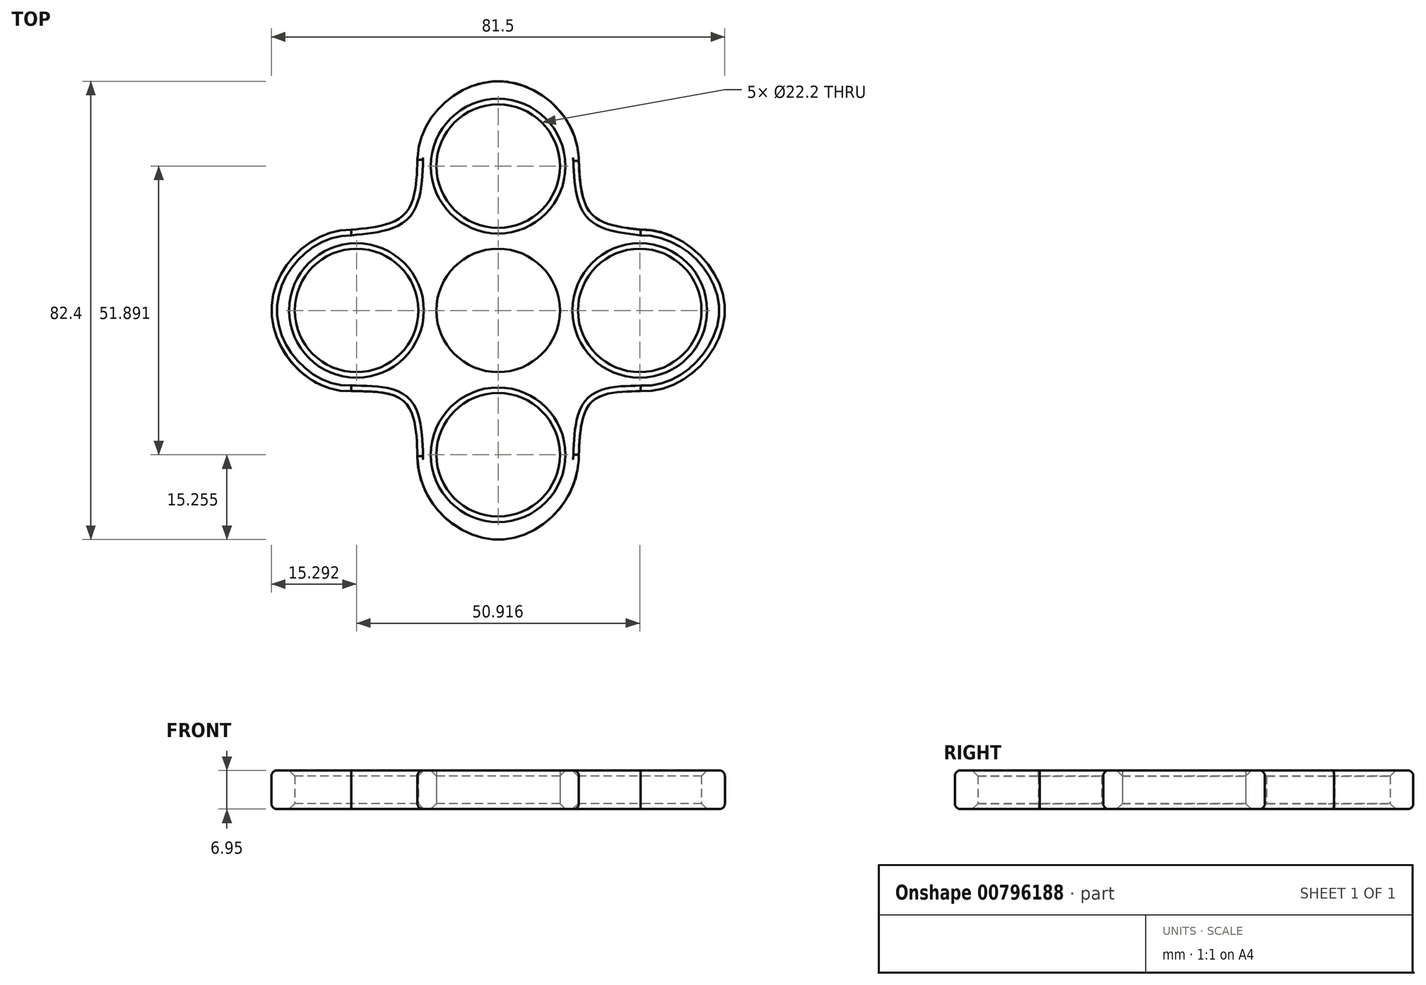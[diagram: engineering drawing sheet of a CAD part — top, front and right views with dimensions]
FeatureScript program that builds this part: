
annotation { "Feature Type Name" : "Feature", "Feature Type Description" : "" }
export const myFeature = defineFeature(function(context is Context, id is Id, definition is map)
    precondition{}
    {
        {
            var Q0;
            Q0=qCreatedBy(makeId("Top.planeOp"),FACE);
            var sketch = newSketch(context, id + "F0", { "sketchPlane" : qUnion([Q0])});
            skCircle(sketch, "E0", {"center": v(0, 0) * mm, "radius": 11.1 * mm});
            skCircle(sketch, "E1", {"center": v(-25.46, 0) * mm, "radius": 11.1 * mm});
            skCircle(sketch, "E2.MirrorC", {"center": v(25.46, 0) * mm, "radius": 11.1 * mm});
            skCircle(sketch, "E3", {"center": v(0, 25.95) * mm, "radius": 11.1 * mm});
            skCircle(sketch, "E4.MirrorC", {"center": v(0, -25.95) * mm, "radius": 11.1 * mm});
            skSolve(sketch);
        }
        {
            var Q0;
            Q0=qCreatedBy(makeId("Top.planeOp"),FACE);
            var sketch = newSketch(context, id + "F1", { "sketchPlane" : qUnion([Q0])});
            skPoint(sketch, "E5", {"position": v(-26.41, 14.52) * mm});
            skPoint(sketch, "E6", {"position": v(25.62, 14.52) * mm});
            skPoint(sketch, "E7.MirrorP", {"position": v(-26.41, -14.52) * mm});
            skPoint(sketch, "E8.MirrorP", {"position": v(25.62, -14.52) * mm});
            skPoint(sketch, "E9", {"position": v(0, 41.2) * mm});
            skPoint(sketch, "E10.MirrorP", {"position": v(0, -41.2) * mm});
            skPoint(sketch, "E11", {"position": v(-40.75, 0) * mm});
            skPoint(sketch, "E12.MirrorP", {"position": v(40.75, 0) * mm});
            skPoint(sketch, "E13", {"position": v(14.49, 27.53) * mm});
            skPoint(sketch, "E14", {"position": v(14.49, -26.88) * mm});
            skPoint(sketch, "E15.MirrorP", {"position": v(-14.49, 27.53) * mm});
            skPoint(sketch, "E16.MirrorP", {"position": v(-14.49, -26.88) * mm});
            skPoint(sketch, "E17", {"position": v(-10.43, 9.88) * mm});
            skPoint(sketch, "E18", {"position": v(10.75, 9.88) * mm});
            skPoint(sketch, "E19", {"position": v(-10.43, -8.6) * mm});
            skPoint(sketch, "E20", {"position": v(10.75, -8.4) * mm});
            skFitSpline(sketch, "E21", {"points": [v(-40.75, 0) * mm, v(-26.41, 14.52) * mm, v(-10.43, 9.88) * mm, v(-14.49, 27.53) * mm, v(0, 41.2) * mm, v(14.49, 27.53) * mm, v(10.75, 9.88) * mm, v(25.62, 14.52) * mm, v(40.75, 0) * mm, v(25.62, -14.52) * mm, v(10.75, -8.4) * mm, v(14.49, -26.88) * mm, v(0, -41.2) * mm, v(-14.49, -26.88) * mm, v(-10.43, -8.6) * mm, v(-26.41, -14.52) * mm, v(-40.75, 0) * mm]});
            skPoint(sketch, "E22", {"position": v(16.77, 17.36) * mm});
            skPoint(sketch, "E23", {"position": v(16.77, -16.5) * mm});
            skPoint(sketch, "E24.MirrorP", {"position": v(-16.77, 17.36) * mm});
            skPoint(sketch, "E25.MirrorP", {"position": v(-16.77, -16.5) * mm});
            skFitSpline(sketch, "E26", {"points": [v(-14.49, 27.53) * mm, v(-16.77, 17.36) * mm, v(-26.41, 14.52) * mm], "startDerivative": vector(-0.76, -23.8) * mm, "endDerivative": vector(-23.17, -2.15) * mm});
            skFitSpline(sketch, "E27", {"points": [v(14.49, 27.53) * mm, v(16.77, 17.36) * mm, v(25.62, 14.52) * mm], "startDerivative": vector(0.9, -23.37) * mm, "endDerivative": vector(21.57, -2.46) * mm});
            skFitSpline(sketch, "E28", {"points": [v(-26.41, -14.52) * mm, v(-16.77, -16.5) * mm, v(-14.49, -26.88) * mm], "startDerivative": vector(23.39, -0.02) * mm, "endDerivative": vector(0.61, -24.54) * mm});
            skFitSpline(sketch, "E29", {"points": [v(25.62, -14.52) * mm, v(16.77, -16.5) * mm, v(14.49, -26.88) * mm], "startDerivative": vector(-21.8, -0.3) * mm, "endDerivative": vector(-0.74, -24.1) * mm});
            skSolve(sketch);
        }
        {
            var Q0;
            Q0 = qSketchRegion(id + "F1", true);
            extrude(context, id + "F2", {"entities" : qUnion([Q0]), "depth" : 6.95 * mm, "offsetDistance" : 25.4 * mm});
        }
        {
            var Q0;
            Q0 = qSketchRegion(id + "F0", true);
            extrude(context, id + "F3", {"entities" : qUnion([Q0]), "operationType" : NewBodyOperationType.REMOVE, "endBound" : BoundingType.THROUGH_ALL, "depth" : 25.4 * mm, "offsetDistance" : 25.4 * mm});
        }
        {
            var Q0;
            {var subQ0=sQuery(id+"F1.wireOp",EDGE,"E21");Q0=makeQuery(id+"F2.opExtrude","CAP_EDGE",EDGE,{"disambiguationData":[OSD([subQ0]),TDD([makeQuery(id+"F1.imprint","IMPRINT",EDGE,{"disambiguationData":[TD([[makeQuery(id+"F1.imprint","INTERSECT",VERTEX,{"disambiguationData":[OD(1.0)],"derivedFrom":[subQ0,sQuery(id+"F1.wireOp",EDGE,"E26")]}),1.0]])],"derivedFrom":subQ0})])],"isStart":false});}
            var Q1;
            Q1=makeQuery(id+"F2.opExtrude","CAP_EDGE",EDGE,{"disambiguationData":[OSD([sQuery(id+"F1.wireOp",EDGE,"E26")])],"isStart":false});
            var Q2;
            Q2=makeQuery(id+"F2.opExtrude","CAP_EDGE",EDGE,{"disambiguationData":[OSD([sQuery(id+"F1.wireOp",EDGE,"E28")])],"isStart":false});
            var Q3;
            {var subQ0=sQuery(id+"F1.wireOp",EDGE,"E28");var subQ1=sQuery(id+"F1.wireOp",EDGE,"E21");var subQ2=makeQuery(id+"F1.imprint","INTERSECT",VERTEX,{"disambiguationData":[OD(1.0)],"derivedFrom":[subQ1,subQ0]});var subQ3=sQuery(id+"F1.wireOp",EDGE,"E29");var subQ4=makeQuery(id+"F1.imprint","INTERSECT",VERTEX,{"disambiguationData":[OD(1.0)],"derivedFrom":[subQ1,subQ3]});Q3=makeQuery(id+"F2.opExtrude","CAP_EDGE",EDGE,{"disambiguationData":[OSD([subQ1]),TDD([makeQuery(id+"F1.imprint","IMPRINT",EDGE,{"disambiguationData":[TD([[subQ4,1.0]])],"derivedFrom":subQ1}),makeQuery(id+"F1.imprint","IMPRINT",EDGE,{"disambiguationData":[TD([[subQ2,1.0]])],"derivedFrom":subQ1}),makeQuery(id+"F1.imprint","IMPRINT",EDGE,{"disambiguationData":[TD([[subQ2,-1.0]])],"derivedFrom":subQ1})])],"isStart":false});}
            var Q4;
            Q4=makeQuery(id+"F2.opExtrude","CAP_EDGE",EDGE,{"disambiguationData":[OSD([sQuery(id+"F1.wireOp",EDGE,"E29")])],"isStart":false});
            var Q5;
            {var subQ0=sQuery(id+"F1.wireOp",EDGE,"E21");Q5=makeQuery(id+"F2.opExtrude","CAP_EDGE",EDGE,{"disambiguationData":[OSD([subQ0]),TDD([makeQuery(id+"F1.imprint","IMPRINT",EDGE,{"disambiguationData":[TD([[makeQuery(id+"F1.imprint","INTERSECT",VERTEX,{"disambiguationData":[OD(1.0)],"derivedFrom":[subQ0,sQuery(id+"F1.wireOp",EDGE,"E27")]}),-1.0]])],"derivedFrom":subQ0})])],"isStart":false});}
            var Q6;
            Q6=makeQuery(id+"F2.opExtrude","CAP_EDGE",EDGE,{"disambiguationData":[OSD([sQuery(id+"F1.wireOp",EDGE,"E27")])],"isStart":false});
            var Q7;
            {var subQ0=sQuery(id+"F1.wireOp",EDGE,"E27");var subQ1=sQuery(id+"F1.wireOp",EDGE,"E21");var subQ2=makeQuery(id+"F1.imprint","INTERSECT",VERTEX,{"disambiguationData":[OD(0.0)],"derivedFrom":[subQ1,subQ0]});var subQ3=sQuery(id+"F1.wireOp",EDGE,"E26");var subQ4=makeQuery(id+"F1.imprint","INTERSECT",VERTEX,{"disambiguationData":[OD(0.0)],"derivedFrom":[subQ1,subQ3]});Q7=makeQuery(id+"F2.opExtrude","CAP_EDGE",EDGE,{"disambiguationData":[OSD([subQ1]),TDD([makeQuery(id+"F1.imprint","IMPRINT",EDGE,{"disambiguationData":[TD([[subQ4,1.0]])],"derivedFrom":subQ1}),makeQuery(id+"F1.imprint","IMPRINT",EDGE,{"disambiguationData":[TD([[subQ4,-1.0]])],"derivedFrom":subQ1}),makeQuery(id+"F1.imprint","IMPRINT",EDGE,{"disambiguationData":[TD([[subQ2,-1.0]])],"derivedFrom":subQ1})])],"isStart":false});}
            fillet(context, id + "F4", {"entities" : qUnion([Q0, Q1, Q2, Q3, Q4, Q5, Q6, Q7]), "radius" : 1 * mm, "tangentPropagation" : true, "allowEdgeOverflow" : false});
        }
        {
            var Q0;
            {var subQ0=sQuery(id+"F1.wireOp",EDGE,"E21");Q0=makeQuery(id+"F2.opExtrude","CAP_EDGE",EDGE,{"disambiguationData":[OSD([subQ0]),TDD([makeQuery(id+"F1.imprint","IMPRINT",EDGE,{"disambiguationData":[TD([[makeQuery(id+"F1.imprint","INTERSECT",VERTEX,{"disambiguationData":[OD(1.0)],"derivedFrom":[subQ0,sQuery(id+"F1.wireOp",EDGE,"E26")]}),1.0]])],"derivedFrom":subQ0})])],"isStart":true});}
            var Q1;
            Q1=makeQuery(id+"F2.opExtrude","CAP_EDGE",EDGE,{"disambiguationData":[OSD([sQuery(id+"F1.wireOp",EDGE,"E28")])],"isStart":true});
            var Q2;
            {var subQ0=sQuery(id+"F1.wireOp",EDGE,"E28");var subQ1=sQuery(id+"F1.wireOp",EDGE,"E21");var subQ2=makeQuery(id+"F1.imprint","INTERSECT",VERTEX,{"disambiguationData":[OD(1.0)],"derivedFrom":[subQ1,subQ0]});var subQ3=sQuery(id+"F1.wireOp",EDGE,"E29");var subQ4=makeQuery(id+"F1.imprint","INTERSECT",VERTEX,{"disambiguationData":[OD(1.0)],"derivedFrom":[subQ1,subQ3]});Q2=makeQuery(id+"F2.opExtrude","CAP_EDGE",EDGE,{"disambiguationData":[OSD([subQ1]),TDD([makeQuery(id+"F1.imprint","IMPRINT",EDGE,{"disambiguationData":[TD([[subQ4,1.0]])],"derivedFrom":subQ1}),makeQuery(id+"F1.imprint","IMPRINT",EDGE,{"disambiguationData":[TD([[subQ2,1.0]])],"derivedFrom":subQ1}),makeQuery(id+"F1.imprint","IMPRINT",EDGE,{"disambiguationData":[TD([[subQ2,-1.0]])],"derivedFrom":subQ1})])],"isStart":true});}
            var Q3;
            Q3=makeQuery(id+"F2.opExtrude","CAP_EDGE",EDGE,{"disambiguationData":[OSD([sQuery(id+"F1.wireOp",EDGE,"E29")])],"isStart":true});
            var Q4;
            {var subQ0=sQuery(id+"F1.wireOp",EDGE,"E21");Q4=makeQuery(id+"F2.opExtrude","CAP_EDGE",EDGE,{"disambiguationData":[OSD([subQ0]),TDD([makeQuery(id+"F1.imprint","IMPRINT",EDGE,{"disambiguationData":[TD([[makeQuery(id+"F1.imprint","INTERSECT",VERTEX,{"disambiguationData":[OD(1.0)],"derivedFrom":[subQ0,sQuery(id+"F1.wireOp",EDGE,"E27")]}),-1.0]])],"derivedFrom":subQ0})])],"isStart":true});}
            var Q5;
            Q5=makeQuery(id+"F2.opExtrude","CAP_EDGE",EDGE,{"disambiguationData":[OSD([sQuery(id+"F1.wireOp",EDGE,"E27")])],"isStart":true});
            var Q6;
            {var subQ0=sQuery(id+"F1.wireOp",EDGE,"E27");var subQ1=sQuery(id+"F1.wireOp",EDGE,"E21");var subQ2=makeQuery(id+"F1.imprint","INTERSECT",VERTEX,{"disambiguationData":[OD(0.0)],"derivedFrom":[subQ1,subQ0]});var subQ3=sQuery(id+"F1.wireOp",EDGE,"E26");var subQ4=makeQuery(id+"F1.imprint","INTERSECT",VERTEX,{"disambiguationData":[OD(0.0)],"derivedFrom":[subQ1,subQ3]});Q6=makeQuery(id+"F2.opExtrude","CAP_EDGE",EDGE,{"disambiguationData":[OSD([subQ1]),TDD([makeQuery(id+"F1.imprint","IMPRINT",EDGE,{"disambiguationData":[TD([[subQ4,1.0]])],"derivedFrom":subQ1}),makeQuery(id+"F1.imprint","IMPRINT",EDGE,{"disambiguationData":[TD([[subQ4,-1.0]])],"derivedFrom":subQ1}),makeQuery(id+"F1.imprint","IMPRINT",EDGE,{"disambiguationData":[TD([[subQ2,-1.0]])],"derivedFrom":subQ1})])],"isStart":true});}
            var Q7;
            Q7=makeQuery(id+"F2.opExtrude","CAP_EDGE",EDGE,{"disambiguationData":[OSD([sQuery(id+"F1.wireOp",EDGE,"E26")])],"isStart":true});
            fillet(context, id + "F5", {"entities" : qUnion([Q0, Q1, Q2, Q3, Q4, Q5, Q6, Q7]), "radius" : 1 * mm, "tangentPropagation" : true, "allowEdgeOverflow" : false});
        }
        {
            var Q0;
            Q0=makeQuery(id+"F3.boolean.opBoolean","INTERSECT",EDGE,{"derivedFrom":[makeQuery(id+"F2.opExtrude","CAP_FACE",FACE,{"disambiguationData":[OSD([sQuery(id+"F1.wireOp",EDGE,"E21"),sQuery(id+"F1.wireOp",EDGE,"E26"),sQuery(id+"F1.wireOp",EDGE,"E27"),sQuery(id+"F1.wireOp",EDGE,"E28"),sQuery(id+"F1.wireOp",EDGE,"E29")])],"isStart":false}),makeQuery(id+"F3.opExtrude","SWEPT_FACE",FACE,{"disambiguationData":[OSD([sQuery(id+"F0.wireOp",EDGE,"E0")])]})]});
            var Q1;
            Q1=makeQuery(id+"F3.boolean.opBoolean","COPY",FACE,{"derivedFrom":makeQuery(id+"F3.opExtrude","SWEPT_FACE",FACE,{"disambiguationData":[OSD([sQuery(id+"F0.wireOp",EDGE,"E1")])]})});
            var Q2;
            Q2=makeQuery(id+"F3.boolean.opBoolean","COPY",FACE,{"derivedFrom":makeQuery(id+"F3.opExtrude","SWEPT_FACE",FACE,{"disambiguationData":[OSD([sQuery(id+"F0.wireOp",EDGE,"E3")])]})});
            var Q3;
            Q3=makeQuery(id+"F3.boolean.opBoolean","COPY",FACE,{"derivedFrom":makeQuery(id+"F3.opExtrude","SWEPT_FACE",FACE,{"disambiguationData":[OSD([sQuery(id+"F0.wireOp",EDGE,"E2.MirrorC")])]})});
            var Q4;
            Q4=makeQuery(id+"F3.boolean.opBoolean","COPY",FACE,{"derivedFrom":makeQuery(id+"F3.opExtrude","SWEPT_FACE",FACE,{"disambiguationData":[OSD([sQuery(id+"F0.wireOp",EDGE,"E4.MirrorC")])]})});
            var Q5;
            Q5=makeQuery(id+"F3.boolean.opBoolean","COPY",EDGE,{"derivedFrom":makeQuery(id+"F3.opExtrude","CAP_EDGE",EDGE,{"disambiguationData":[OSD([sQuery(id+"F0.wireOp",EDGE,"E0")])],"isStart":true})});
            chamfer(context, id + "F6", {"entities" : qUnion([Q0, Q1, Q2, Q3, Q4, Q5]), "width" : 1 * mm, "tangentPropagation" : true});
        }
    });
